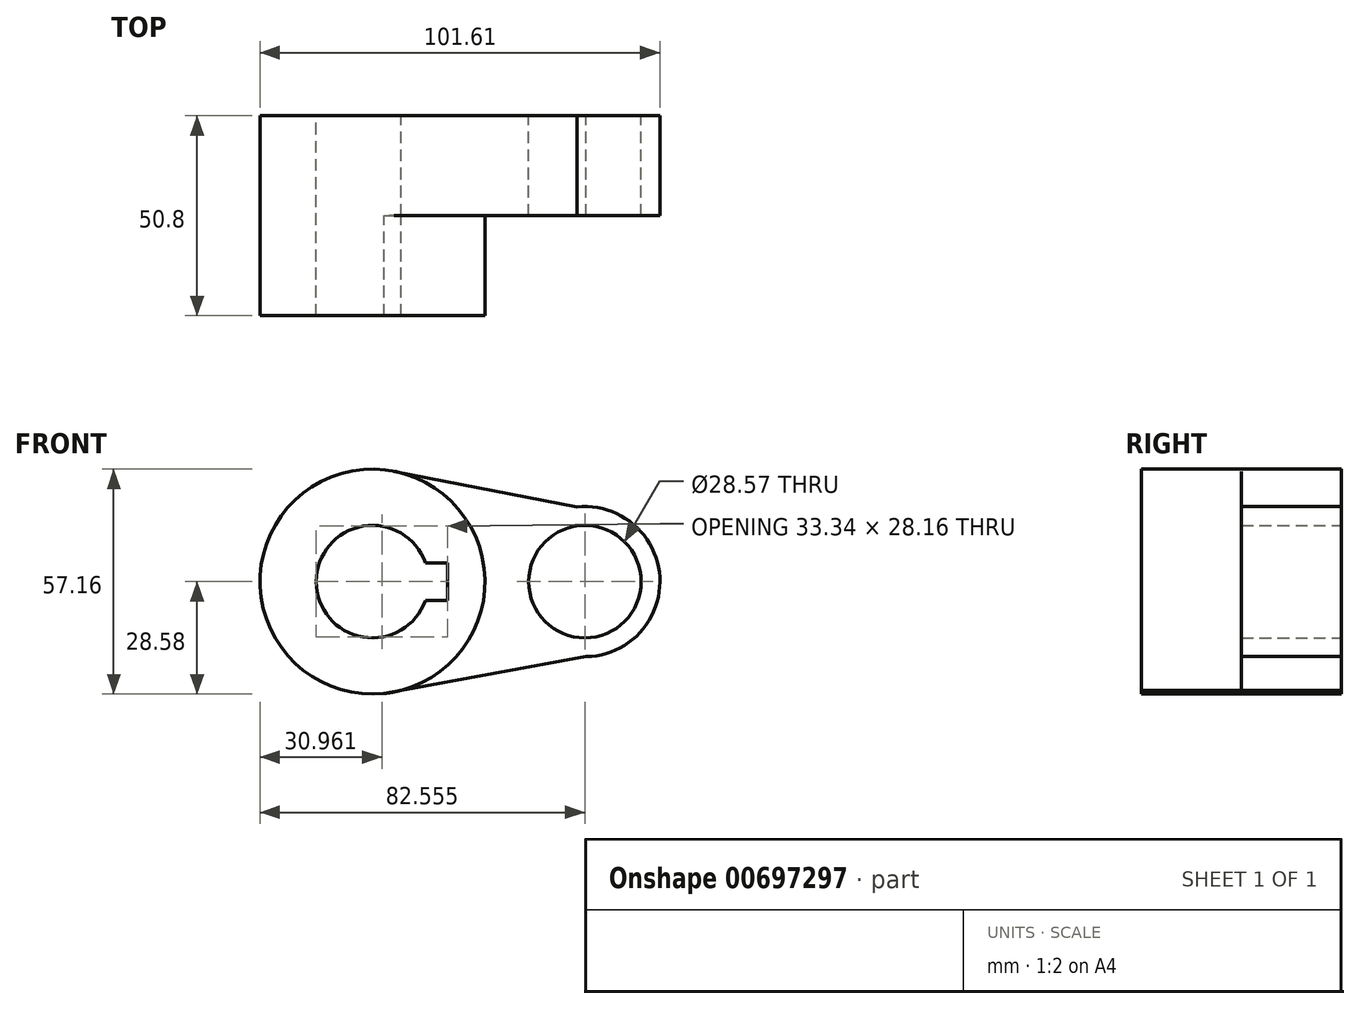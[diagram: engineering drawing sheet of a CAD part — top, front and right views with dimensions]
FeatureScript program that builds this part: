
annotation { "Feature Type Name" : "Feature", "Feature Type Description" : "" }
export const myFeature = defineFeature(function(context is Context, id is Id, definition is map)
    precondition{}
    {
        {
            var Q0;
            Q0=qCreatedBy(makeId("Front.planeOp"),FACE);
            var sketch = newSketch(context, id + "F0", { "sketchPlane" : qUnion([Q0])});
            skCircle(sketch, "E0", {"center": v(0, 0) * mm, "radius": 28.57 * mm});
            skCircle(sketch, "E1", {"center": v(53.98, 0) * mm, "radius": 19.05 * mm});
            skLineSegment(sketch, "E2", {"start": v(5.49, 28.04) * mm, "end": v(51.99, 18.95) * mm});
            skLineSegment(sketch, "E3", {"start": v(2.96, -28.42) * mm, "end": v(54.31, -19.05) * mm});
            skCircle(sketch, "E4", {"center": v(0, 0) * mm, "radius": 14.29 * mm});
            skCircle(sketch, "E5", {"center": v(53.98, 0) * mm, "radius": 14.29 * mm});
            skLineSegment(sketch, "E6.bottom", {"start": v(-19.05, 4.76) * mm, "end": v(19.05, 4.76) * mm});
            skLineSegment(sketch, "E6.top", {"start": v(-19.05, -4.76) * mm, "end": v(19.05, -4.76) * mm});
            skLineSegment(sketch, "E6.left", {"start": v(-19.05, 4.76) * mm, "end": v(-19.05, -4.76) * mm});
            skLineSegment(sketch, "E6.right", {"start": v(19.05, 4.76) * mm, "end": v(19.05, -4.76) * mm});
            skSolve(sketch);
        }
        {
            var Q0;
            Q0 = qSketchRegion(id + "F0", true);
            extrude(context, id + "F1", {"entities" : qUnion([Q0]), "depth" : 25.4 * mm, "offsetDistance" : 25.4 * mm});
        }
        {
            var Q0;
            {var subQ5=sQuery(id+"F0.wireOp",EDGE,"E6.left");Q0=makeQuery(id+"F0.imprint","IMPRINT",FACE,{"disambiguationData":[TD([[makeQuery(id+"F0.imprint","IMPRINT",EDGE,{"derivedFrom":subQ5}),1.0]])]});}
            var Q1;
            {var subQ4=sQuery(id+"F0.wireOp",EDGE,"E6.left");Q1=makeQuery(id+"F0.imprint","IMPRINT",FACE,{"disambiguationData":[TD([[makeQuery(id+"F0.imprint","IMPRINT",EDGE,{"derivedFrom":subQ4}),-1.0]])]});}
            extrude(context, id + "F2", {"entities" : qUnion([Q0, Q1]), "operationType" : NewBodyOperationType.ADD, "depth" : 50.8 * mm, "offsetDistance" : 25.4 * mm});
        }
    });
